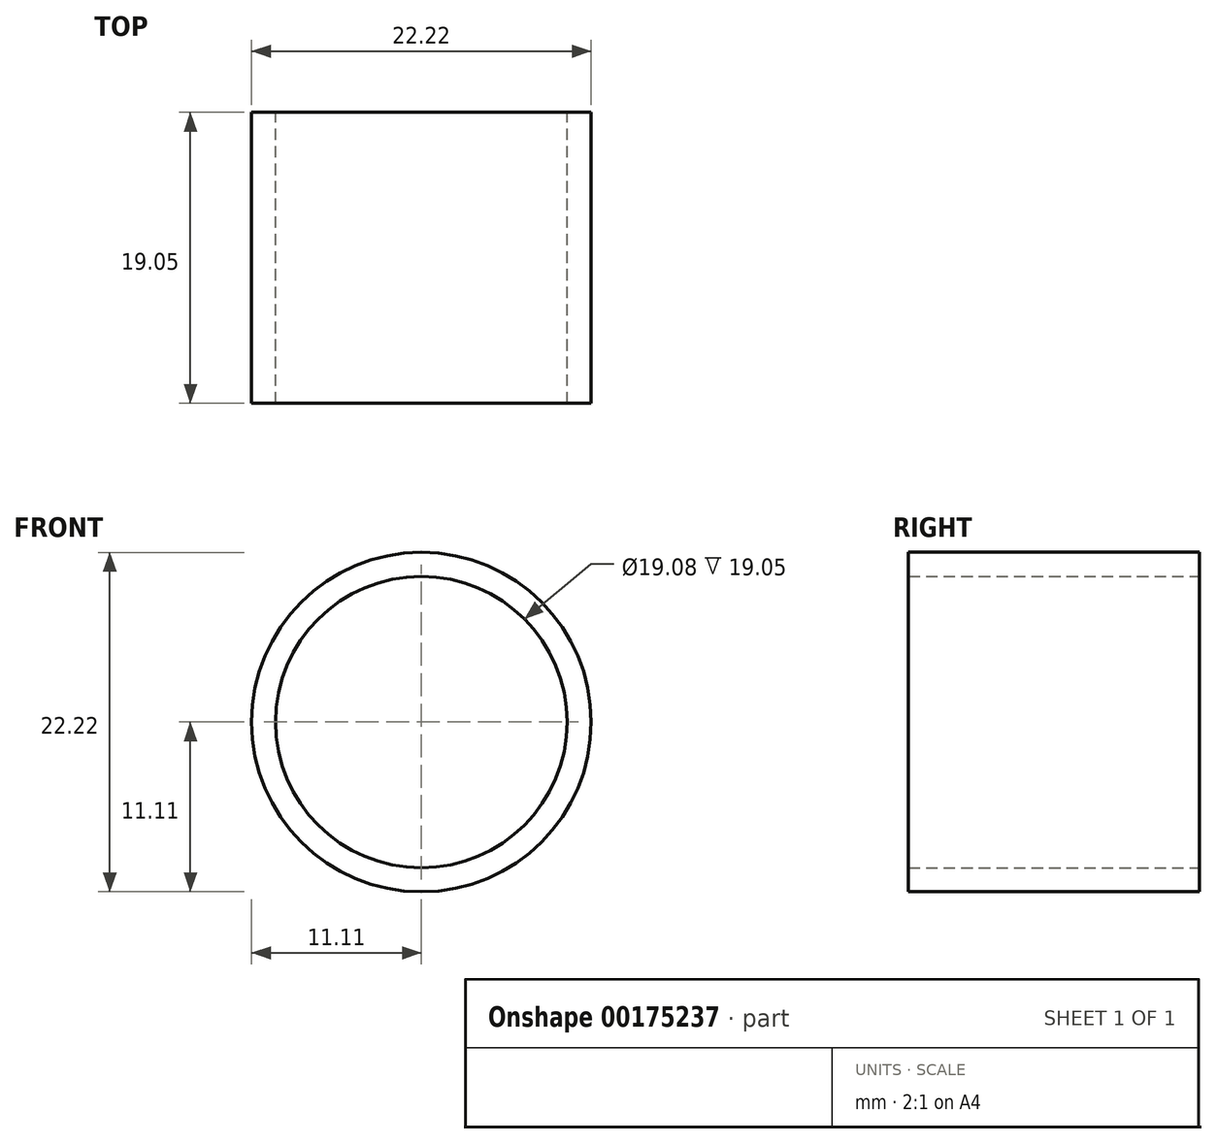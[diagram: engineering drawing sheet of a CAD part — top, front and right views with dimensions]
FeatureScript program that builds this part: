
annotation { "Feature Type Name" : "Feature", "Feature Type Description" : "" }
export const myFeature = defineFeature(function(context is Context, id is Id, definition is map)
    precondition{}
    {
        {
            var Q0;
            Q0=qCreatedBy(makeId("Front.planeOp"),FACE);
            var sketch = newSketch(context, id + "F0", { "sketchPlane" : qUnion([Q0])});
            skCircle(sketch, "E0", {"center": v(0, 0) * mm, "radius": 11.11 * mm});
            skCircle(sketch, "E1", {"center": v(0, 0) * mm, "radius": 9.54 * mm});
            skSolve(sketch);
        }
        {
            var Q0;
            Q0=makeQuery(id+"F0.imprint","IMPRINT",FACE,{"disambiguationData":[TD([[makeQuery(id+"F0.imprint","IMPRINT",EDGE,{"derivedFrom":sQuery(id+"F0.wireOp",EDGE,"E0")}),1.0]])]});
            extrude(context, id + "F1", {"entities" : qUnion([Q0]), "depth" : 19.05 * mm});
        }
    });
